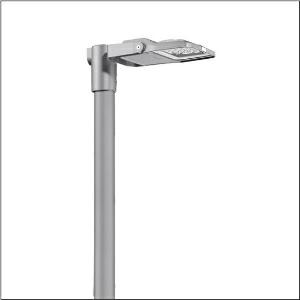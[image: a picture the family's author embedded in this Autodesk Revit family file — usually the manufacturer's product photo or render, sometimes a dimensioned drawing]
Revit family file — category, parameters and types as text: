
# Revit family: floodlight_fl_21_iq_micro___pl61_5xa7761a2c3a_df0f
name_source: partatom
category: Lighting Fixtures
units: mm (PartAtom-declared; Revit-internal decimal feet)

## family parameters
Cut with Voids When Loaded = No
Host = Face
Light Source = No
Part Type = Normal
Room Calculation Point = No
Round Connector Dimension = Use Diameter
Shared = No

## types (1)
- --- (1 x LED, 2910 lm, 23.1 W, 3000K)
    Apparent Load = 23 VA
    CIE Flux Codes = 33 65 98 100 100
    Color Rendering = 70
    Color Temperature = 3000K
    Default Elevation = 1800 mm
    Description = Floodlight FL 21 iQ micro, floodlight, primary light control with lens, of PMMA, primary optical cover: protective disc, of toughened safety glass, transparent, light distribution: PL61, light emission: direct distribution, installation type: surface-mounted, LED, High Power LED, rated luminous flux: 2.910lm, luminous efficacy: 126lm/W, light colour: 730, colour temperature: 3000K, control: optimised constant luminous flux control (CLO 2.0), Desk-Remote (wireless, voltage-free reading and setting of iQ features in the workshop via application-optimized NFC function/RFID function), Light-Fading, Smart-Wire, Night-Set, Lumen-Switch, Temp-Guard, Auto-Match, with terminal, 6-pole, mains connection: 220..240V, AC, 50/60Hz, start of lifetime: 23W, end of service life: 24W, reduction: 11W, luminaire housing, of diecast aluminium, powder-coated, Siteco® metallic grey (DB 702S), corrosivity category C5 mid according to DIN EN ISO 12944, sealing non-destructively replaceable, please order mast flange separately, mast bracket, of steel, galvanised, powder-coated, Siteco® metallic grey (DB 702S), protection rating (complete): IP66, insulation class (complete): insulation class II (safety insulation), certification: CE, ENEC, VDE, protection symbol: D, impact resistance: IK07, permissible operating ambient temperature: -40..+40°C, permissible operating ambient temperature for outdoor applications: -40..+50°C, standard: DIN EN 12944, LABS conformity tested according to VDMA 24364:2018-05, packaging unit: 1 piece

Light Distribution: PL61
    Height = 65 mm
    Lamp = 1 x LED
    Lamp Light Flux = 2910 lm
    Lamp Power = 23.1 W
    Lamp count = 1
    Length = 312 mm
    Luminous efficacy = 126 lm/W
    Manufacturer = Siteco
    ModVariant = No
    Model = 5XA7761A2C3A
    Number of Poles = 1
    OnlyDefault = Yes
    Power Factor = 1
    Product Name = Floodlight FL 21 iQ micro | PL61
    Product group = floodlight | pylon top
    ProductGroupID = 6101
    Protection Class = Protection class II
    Protection Degree = IP 66
    RLX_Detail_Level = 1
    RLX_Emergency_Light_Flux = 0 lm
    RLX_Emergency_Type = 0
    RLX_Emergency_Type_DB = No
    RlxData = <blob elided: 101909 chars, md5=1cfd7f54>
    Socket = socket
    Standby Power = 0 W
    System Light Flux = 2910 lm
    System Power = 23 W
    Type Comments = factory setting: luminous flux: 100 % | dim-lin: 254 | 455 mA
    Type Image = l_1007121.jpg
    URL = http://relux.com
    VarID = @adj_147265
    Voltage = 0 V
    Weight = 0.00 kg
    Width = 230 mm

## geometry (parser evidence)
native form markers: Blend x4, Sweep x12
no freeform markers — native parametric forms only
